# Revit family: Hager-VOLTA-Surface_mounted-IP30-Without_Cover-With_DIN-Hosted-PL-pl
name_source: partatom
category: Electrical Equipment
units: mm (PartAtom-declared; Revit-internal decimal feet)

## family parameters
Cut with Voids When Loaded = No
Host = Face
Maintain Annotation Orientation = Yes
Panel Configuration = Two Columns, Circuits Across
Part Type = Panelboard
Room Calculation Point = No
Round Connector Dimension = Use Diameter
Shared = No

## types (8) — shared parameters
BC_MODEL_ID = 1547267
BC_OBJECT_ID = 513503
BC_OBJECT_VERSION = #5
Code hager = ADD-EC000214_EU
EF000003 - Sposób montażu = Montaż natynkowy
EF000024 - Odporność na promieniowanie UV = No
EF000049 - Głębokość = 96 mm  [stored 0.314961 ft]
EF000116 - Numer RAL = 9010
EF000118 - Z płytą montażową = No
EF001062 - Wykonanie zgodne z Dyrektywą Kompatybilności Elektromagnetycznej EMC = No
EF001134 - Szyna DIN = Yes
EF002950 - Szerokość wyrażona liczbą modułów = 12
EF005474 - Stopień ochrony (IP) = IP30
EF006244 - Transparentna pokrywa/drzwi = No
EF006306 - Z zamkiem = No
EF015941 - Drzwi przepuszczające sygnał = No
ETIM class code = EC000214
ETIM class name = Small distribution board
HG000001-Number of columns-pl = 1
HG000002-with door or cover-pl = No
HG000003-Range-pl = VOLTA
HG000005-Thickness-pl = 2 mm  [stored 0.00656168 ft]
HG000006-Flush mounted-pl = No
HG000009-Double swing door-pl = No
HG000010-Asymmetric doors-pl = No
HG000011-Empty rows from bottom-pl = No
HG000012-Door swing angle-pl = 90.00°
HG000013-Door on the left-pl = No
HG000014-Door on the right-pl = Yes
HG000015-Clearance visibility-pl = Yes
HG000016-Door 3D visibility-pl = Yes
HG000017-Distance between poles-pl = 18 mm  [stored 0.0590551 ft]
HG000060-RAL-number = 9010
HG000099-Onfly Template ID-pl-PL = 507532
HGEF0002950-Szerokość wyrażona liczbą modułów = 12
Manufacturer = Hager
Name = VOLTA-Surface_mounted-IP30-Without_Cover-With_DIN-PL
Name BIM&CO = Electricity
Name hager = ADD_Enclosures_EC000214
Uniformat = Low Tension Service & Dist.
Uniformat code = D501001
zero-valued in all types: Default Elevation, EF000218 - Głębokość wbudowania, EF000332 - Wysokość wbudowania, EF000846 - Szerokość wbudowania, EF001131 - Głębokość wewnętrzna, HG000007-Number of empty columns-pl, HG000008-Number of empty rows-pl

## per-type parameters (varying)
| type | BC_VARIANT_ID | EF000007 - Kolor | EF000008 - Szerokość | EF000040 - Wysokość | EF000266 - Liczba rzędów | EF001088 - Możliwość rozbudowy | EF009212 - Wykonanie/rodzaj pokrywy | EF015776 - Listwa zaciskowa uziemienia | EF015777 - Listwa zaciskowa przewodu neutralnego | HG000004-Manufacturer reference-pl | HGEF000266-Liczba rzędów |
| VOLTA-Surface_mounted_W348_H245_D96_12_Modular_Spacing-VA12B | 1174364 | Biały | 348 mm  [stored 1.14173 ft] | 245 mm  [stored 0.803806 ft] | 1 | Yes | Z otworem | Yes | Yes | VA12B | 1 |
| VOLTA-Surface_mounted_W305_H245_D96_12_Modular_Spacing-VA12BN | 1174367 |  | 305 mm  [stored 1.00066 ft] | 245 mm  [stored 0.803806 ft] | 1 | No |  | No | No | VA12BN | 1 |
| VOLTA-Surface_mounted_W305_H370_D96_12_Modular_Spacing-VA24B | 1174369 | Biały | 305 mm  [stored 1.00066 ft] | 370 mm  [stored 1.21391 ft] | 2 | Yes | Z otworem | Yes | Yes | VA24B | 2 |
| VOLTA-Surface_mounted_W305_H370_D96_12_Modular_Spacing-VA24BN | 1174371 | Biały | 305 mm  [stored 1.00066 ft] | 370 mm  [stored 1.21391 ft] | 2 | Yes | Z otworem | Yes | Yes | VA24BN | 2 |
| VOLTA-Surface_mounted_W305_H515_D96_12_Modular_Spacing-VA36B | 1174372 | Biały | 305 mm  [stored 1.00066 ft] | 515 mm  [stored 1.68963 ft] | 3 | Yes | Z otworem | Yes | Yes | VA36B | 3 |
| VOLTA-Surface_mounted_W305_H515_D96_12_Modular_Spacing-VA36BN | 1174373 | Biały | 305 mm  [stored 1.00066 ft] | 515 mm  [stored 1.68963 ft] | 3 | Yes | Z otworem | Yes | Yes | VA36BN | 3 |
| VOLTA-Surface_mounted_W305_H640_D96_12_Modular_Spacing-VA48B | 1174374 | Biały | 305 mm  [stored 1.00066 ft] | 640 mm  [stored 2.09974 ft] | 4 | Yes | Z otworem | Yes | Yes | VA48B | 4 |
| VOLTA-Surface_mounted_W305_H640_D96_12_Modular_Spacing-VA48BN | 1174375 | Biały | 305 mm  [stored 1.00066 ft] | 640 mm  [stored 2.09974 ft] | 4 | Yes | Z otworem | Yes | Yes | VA48BN | 4 |

note: column(s) folded — value = type name in every type: Reference

note: [stored X ft] marks values corroborated as IEEE doubles in the binary element streams (Revit-internal decimal feet)

## geometry (parser evidence)
native form markers: Sweep x14
no freeform markers — native parametric forms only
